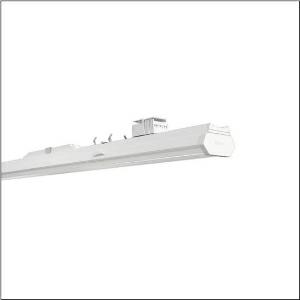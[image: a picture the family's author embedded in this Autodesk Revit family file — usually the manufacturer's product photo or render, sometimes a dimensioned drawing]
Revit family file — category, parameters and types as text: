
# Revit family: licross_r__11_protected_mo_51tp12cn685g_00be
name_source: partatom
category: Lighting Fixtures
units: mm (PartAtom-declared; Revit-internal decimal feet)

## family parameters
Cut with Voids When Loaded = No
Host = Face
Light Source = No
Part Type = Normal
Room Calculation Point = No
Round Connector Dimension = Use Diameter
Shared = No

## types (1)
- --- (1 x LED, 8840 lm, 49.4 W, 6500K)
    Apparent Load = 49 VA
    CIE Flux Codes = 73 92 98 99 100
    Color Rendering = 80
    Color Temperature = 6500K
    Default Elevation = 1800 mm
    Description = Licross® 11 Protected MO, luminaire insert, of sheet steel, galvanised, coil coated, white, length: 1.500mm, width: 90mm, height: 101mm, LED rated luminous flux: 8.840lm, light colour: 865, control gear: ON/OFF Multilumen, CLOi, with plug, 3-pole, with phase selection, mains connection: 220..240V, AC, 50/60Hz, start of lifetime: 49W, end of service life: 55W, halogen-free wiring, primary light control with lens, of plastic, primary optical cover: cover, of PMMA, light emission: direct distribution, primary light characteristic: symmetric, protection rating (complete): IP64, insulation class (complete): insulation class I (protective earthing), certification: CE, ENEC, VDE, UKCA, protection symbol: D if used in an environment with conductive dust loads with corresponding accessories, impact resistance: IK06, permissible ambient temperature for indoor applications: -35..+40°C, corresponds to IFS (International Featured Standards) requirements for safety and quality in the food industry, reducing of maximum allowable ambient temperature of 5°C with ceiling mounting, LABS conformity tested according to VDMA 24364:2018-05, packaging unit: 1 piece
    Height = 92 mm
    Lamp = 1 x LED
    Lamp Light Flux = 8840 lm
    Lamp Power = 49.4 W
    Lamp count = 1
    Length = 1500 mm
    Luminous efficacy = 179 lm/W
    Manufacturer = Siteco
    ModVariant = No
    Model = 51TP12CN685G
    Mounting Place = Ceiling
    Mounting Type = Pendant
    Number of Poles = 1
    OnlyDefault = Yes
    Power Factor = 1
    Product Name = Licross® 11 Protected MO
    Product group = luminaire insert
    ProductGroupID = 902
    Protection Class = Protection class I
    Protection Degree = IP 64
    RLX_Detail_Level = 1
    RLX_Emergency_Light_Flux = 0 lm
    RLX_Emergency_Type = 0
    RLX_Emergency_Type_DB = No
    RlxData = <blob elided: 22121 chars, md5=aa7b9206>
    Socket = socket
    Standby Power = 0 W
    System Light Flux = 8840 lm
    System Power = 49 W
    Type Comments = factory setting: luminous flux: 100 % | (A | C | E) | 113 mA
    Type Image = l_1256148.jpg
    URL = http://relux.com
    VarID = @adj_010533
    Voltage = 0 V
    Weight = 0.00 kg
    Width = 88 mm

## geometry (parser evidence)
native form markers: Blend x4, Sweep x11
no freeform markers — native parametric forms only
